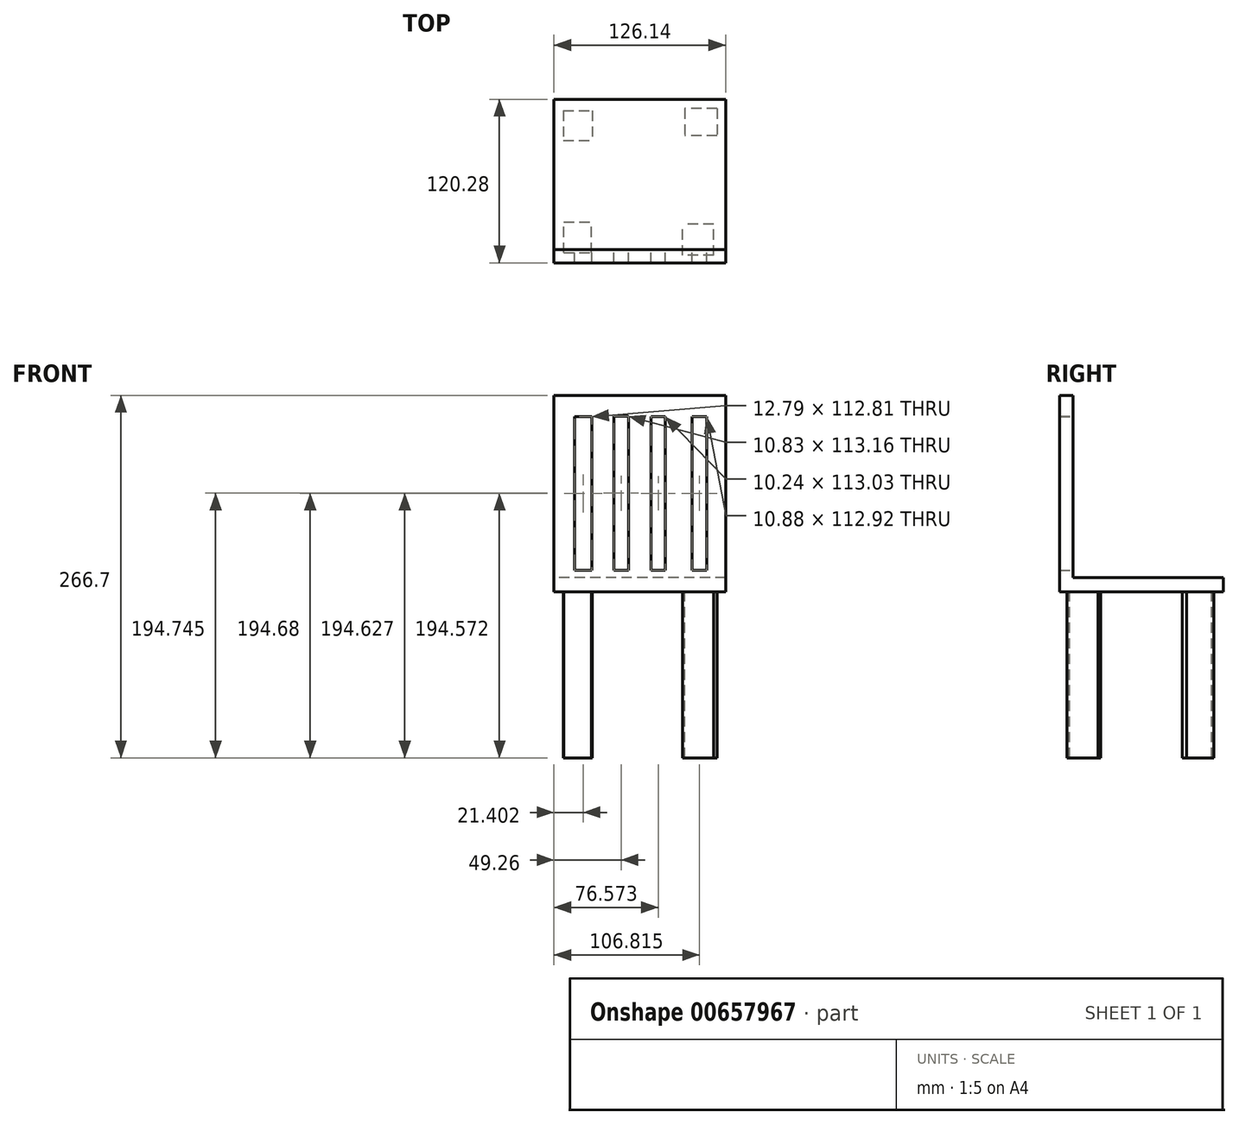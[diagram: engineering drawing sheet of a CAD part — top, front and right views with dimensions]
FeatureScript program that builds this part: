
annotation { "Feature Type Name" : "Feature", "Feature Type Description" : "" }
export const myFeature = defineFeature(function(context is Context, id is Id, definition is map)
    precondition{}
    {
        {
            var Q0;
            Q0=qCreatedBy(makeId("Top.planeOp"),FACE);
            var sketch = newSketch(context, id + "F0", { "sketchPlane" : qUnion([Q0])});
            skLineSegment(sketch, "E0.bottom", {"start": v(63.07, 60.14) * mm, "end": v(-63.07, 60.14) * mm});
            skLineSegment(sketch, "E0.top", {"start": v(63.07, -60.14) * mm, "end": v(-63.07, -60.14) * mm});
            skLineSegment(sketch, "E0.left", {"start": v(63.07, 60.14) * mm, "end": v(63.07, -60.14) * mm});
            skLineSegment(sketch, "E0.right", {"start": v(-63.07, 60.14) * mm, "end": v(-63.07, -60.14) * mm});
            skPoint(sketch, "E0.middle", {"position": v(0, 0) * mm});
            skSolve(sketch);
        }
        {
            var Q0;
            Q0 = qSketchRegion(id + "F0", true);
            extrude(context, id + "F1", {"entities" : qUnion([Q0]), "depth" : 10.4 * mm, "offsetDistance" : 25.4 * mm});
        }
        {
            var Q0;
            Q0=makeQuery(id+"F1.opExtrude","CAP_FACE",FACE,{"disambiguationData":[OSD([sQuery(id+"F0.wireOp",EDGE,"E0.bottom"),sQuery(id+"F0.wireOp",EDGE,"E0.top"),sQuery(id+"F0.wireOp",EDGE,"E0.left"),sQuery(id+"F0.wireOp",EDGE,"E0.right")])],"isStart":true});
            var sketch = newSketch(context, id + "F2", { "sketchPlane" : qUnion([Q0])});
            skLineSegment(sketch, "E1.bottom", {"start": v(-55.93, 52.74) * mm, "end": v(-35.65, 52.74) * mm});
            skLineSegment(sketch, "E1.top", {"start": v(-55.93, 30.09) * mm, "end": v(-35.65, 30.09) * mm});
            skLineSegment(sketch, "E1.left", {"start": v(-55.93, 52.74) * mm, "end": v(-55.93, 30.09) * mm});
            skLineSegment(sketch, "E1.right", {"start": v(-35.65, 52.74) * mm, "end": v(-35.65, 30.09) * mm});
            skSolve(sketch);
        }
        {
            var Q0;
            Q0 = qSketchRegion(id + "F2", true);
            extrude(context, id + "F3", {"entities" : qUnion([Q0]), "operationType" : NewBodyOperationType.ADD, "depth" : 122.17 * mm, "offsetDistance" : 25.4 * mm});
        }
        {
            var Q0;
            Q0=makeQuery(id+"F1.opExtrude","CAP_FACE",FACE,{"disambiguationData":[OSD([sQuery(id+"F0.wireOp",EDGE,"E0.bottom"),sQuery(id+"F0.wireOp",EDGE,"E0.top"),sQuery(id+"F0.wireOp",EDGE,"E0.left"),sQuery(id+"F0.wireOp",EDGE,"E0.right")])],"isStart":true});
            var sketch = newSketch(context, id + "F4", { "sketchPlane" : qUnion([Q0])});
            skLineSegment(sketch, "E2.bottom", {"start": v(54.2, 54.62) * mm, "end": v(31.43, 54.62) * mm});
            skLineSegment(sketch, "E2.top", {"start": v(54.2, 31.82) * mm, "end": v(31.43, 31.82) * mm});
            skLineSegment(sketch, "E2.left", {"start": v(54.2, 54.62) * mm, "end": v(54.2, 31.82) * mm});
            skLineSegment(sketch, "E2.right", {"start": v(31.43, 54.62) * mm, "end": v(31.43, 31.82) * mm});
            skSolve(sketch);
        }
        {
            var Q0;
            Q0 = qSketchRegion(id + "F4", true);
            extrude(context, id + "F5", {"entities" : qUnion([Q0]), "operationType" : NewBodyOperationType.ADD, "depth" : 122.17 * mm, "offsetDistance" : 25.4 * mm});
        }
        {
            var Q0;
            Q0=makeQuery(id+"F1.opExtrude","CAP_FACE",FACE,{"disambiguationData":[OSD([sQuery(id+"F0.wireOp",EDGE,"E0.bottom"),sQuery(id+"F0.wireOp",EDGE,"E0.top"),sQuery(id+"F0.wireOp",EDGE,"E0.left"),sQuery(id+"F0.wireOp",EDGE,"E0.right")])],"isStart":true});
            var sketch = newSketch(context, id + "F6", { "sketchPlane" : qUnion([Q0])});
            skLineSegment(sketch, "E3.bottom", {"start": v(56.74, -53.28) * mm, "end": v(33, -53.28) * mm});
            skLineSegment(sketch, "E3.top", {"start": v(56.74, -33.26) * mm, "end": v(33, -33.26) * mm});
            skLineSegment(sketch, "E3.left", {"start": v(56.74, -53.28) * mm, "end": v(56.74, -33.26) * mm});
            skLineSegment(sketch, "E3.right", {"start": v(33, -53.28) * mm, "end": v(33, -33.26) * mm});
            skSolve(sketch);
        }
        {
            var Q0;
            Q0 = qSketchRegion(id + "F6", true);
            extrude(context, id + "F7", {"entities" : qUnion([Q0]), "operationType" : NewBodyOperationType.ADD, "depth" : 122.17 * mm, "offsetDistance" : 25.4 * mm});
        }
        {
            var Q0;
            Q0=makeQuery(id+"F1.opExtrude","CAP_FACE",FACE,{"disambiguationData":[OSD([sQuery(id+"F0.wireOp",EDGE,"E0.bottom"),sQuery(id+"F0.wireOp",EDGE,"E0.top"),sQuery(id+"F0.wireOp",EDGE,"E0.left"),sQuery(id+"F0.wireOp",EDGE,"E0.right")])],"isStart":true});
            var sketch = newSketch(context, id + "F8", { "sketchPlane" : qUnion([Q0])});
            skLineSegment(sketch, "E4.bottom", {"start": v(-56.17, -51.71) * mm, "end": v(-34.92, -51.71) * mm});
            skLineSegment(sketch, "E4.top", {"start": v(-56.17, -30.05) * mm, "end": v(-34.92, -30.05) * mm});
            skLineSegment(sketch, "E4.left", {"start": v(-56.17, -51.71) * mm, "end": v(-56.17, -30.05) * mm});
            skLineSegment(sketch, "E4.right", {"start": v(-34.92, -51.71) * mm, "end": v(-34.92, -30.05) * mm});
            skSolve(sketch);
        }
        {
            var Q0;
            Q0 = qSketchRegion(id + "F8", true);
            extrude(context, id + "F9", {"entities" : qUnion([Q0]), "operationType" : NewBodyOperationType.ADD, "depth" : 122.17 * mm, "offsetDistance" : 25.4 * mm});
        }
        {
            var Q0;
            Q0=makeQuery(id+"F1.opExtrude","CAP_FACE",FACE,{"disambiguationData":[OSD([sQuery(id+"F0.wireOp",EDGE,"E0.bottom"),sQuery(id+"F0.wireOp",EDGE,"E0.top"),sQuery(id+"F0.wireOp",EDGE,"E0.left"),sQuery(id+"F0.wireOp",EDGE,"E0.right")])],"isStart":false});
            var sketch = newSketch(context, id + "F10", { "sketchPlane" : qUnion([Q0])});
            skLineSegment(sketch, "E5.bottom", {"start": v(63.07, -60.14) * mm, "end": v(-63.07, -60.14) * mm});
            skLineSegment(sketch, "E5.top", {"start": v(63.07, -50.28) * mm, "end": v(-63.07, -50.28) * mm});
            skLineSegment(sketch, "E5.left", {"start": v(63.07, -60.14) * mm, "end": v(63.07, -50.28) * mm});
            skLineSegment(sketch, "E5.right", {"start": v(-63.07, -60.14) * mm, "end": v(-63.07, -50.28) * mm});
            skSolve(sketch);
        }
        {
            var Q0;
            Q0 = qSketchRegion(id + "F10", true);
            extrude(context, id + "F11", {"entities" : qUnion([Q0]), "operationType" : NewBodyOperationType.ADD, "depth" : 134.11 * mm, "offsetDistance" : 25.4 * mm});
        }
        {
            var Q0;
            Q0=makeQuery(id+"F11.opExtrude","SWEPT_FACE",FACE,{"disambiguationData":[OSD([sQuery(id+"F10.wireOp",EDGE,"E5.top")])]});
            var sketch = newSketch(context, id + "F12", { "sketchPlane" : qUnion([Q0])});
            skLineSegment(sketch, "E6.bottom", {"start": v(-49.18, 128.92) * mm, "end": v(-38.3, 128.92) * mm});
            skLineSegment(sketch, "E6.top", {"start": v(-49.18, 16) * mm, "end": v(-38.3, 16) * mm});
            skLineSegment(sketch, "E6.left", {"start": v(-49.18, 128.92) * mm, "end": v(-49.18, 16) * mm});
            skLineSegment(sketch, "E6.right", {"start": v(-38.3, 128.92) * mm, "end": v(-38.3, 16) * mm});
            skLineSegment(sketch, "E7.bottom", {"start": v(-18.62, 129.02) * mm, "end": v(-8.38, 129.02) * mm});
            skLineSegment(sketch, "E7.top", {"start": v(-18.62, 16) * mm, "end": v(-8.38, 16) * mm});
            skLineSegment(sketch, "E7.left", {"start": v(-18.62, 129.02) * mm, "end": v(-18.62, 16) * mm});
            skLineSegment(sketch, "E7.right", {"start": v(-8.38, 129.02) * mm, "end": v(-8.38, 16) * mm});
            skLineSegment(sketch, "E8.bottom", {"start": v(8.4, 129.15) * mm, "end": v(19.23, 129.15) * mm});
            skLineSegment(sketch, "E8.top", {"start": v(8.4, 16) * mm, "end": v(19.23, 16) * mm});
            skLineSegment(sketch, "E8.left", {"start": v(8.4, 129.15) * mm, "end": v(8.4, 16) * mm});
            skLineSegment(sketch, "E8.right", {"start": v(19.23, 129.15) * mm, "end": v(19.23, 16) * mm});
            skLineSegment(sketch, "E9.bottom", {"start": v(35.27, 128.8) * mm, "end": v(48.06, 128.8) * mm});
            skLineSegment(sketch, "E9.top", {"start": v(35.27, 16) * mm, "end": v(48.06, 16) * mm});
            skLineSegment(sketch, "E9.left", {"start": v(35.27, 128.8) * mm, "end": v(35.27, 16) * mm});
            skLineSegment(sketch, "E9.right", {"start": v(48.06, 128.8) * mm, "end": v(48.06, 16) * mm});
            skSolve(sketch);
        }
        {
            var Q0;
            Q0 = qSketchRegion(id + "F12", true);
            extrude(context, id + "F13", {"entities" : qUnion([Q0]), "operationType" : NewBodyOperationType.REMOVE, "oppositeDirection" : true, "depth" : 25.4 * mm, "offsetDistance" : 25.4 * mm});
        }
    });
